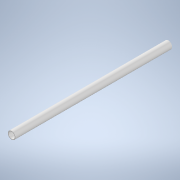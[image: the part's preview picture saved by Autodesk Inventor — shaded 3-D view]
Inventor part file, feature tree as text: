
AUTODESK INVENTOR PART (.ipt)
format: ipt  version: 2020 (Build 240168000, 168)  size: 100,352 bytes
history: native  units: mm
features: extrude x1, fillet x1, sketch x1
ambient origin geometry x8: Origin, YZ Plane, XZ Plane, XY Plane, X Axis, Y Axis, Z Axis, Center Point
bodies: Solid1 (feature_tree)
feature tree (3):
  extrude  "Extrusion1"  Depth=0.5mm
  fillet  "Fillet1"  Radius=520.0mm
  sketch  "Sketch1"  dims[d0=20.0mm d1=2.0mm d2=520.0mm d3=0.0mm d4=0.5mm]
